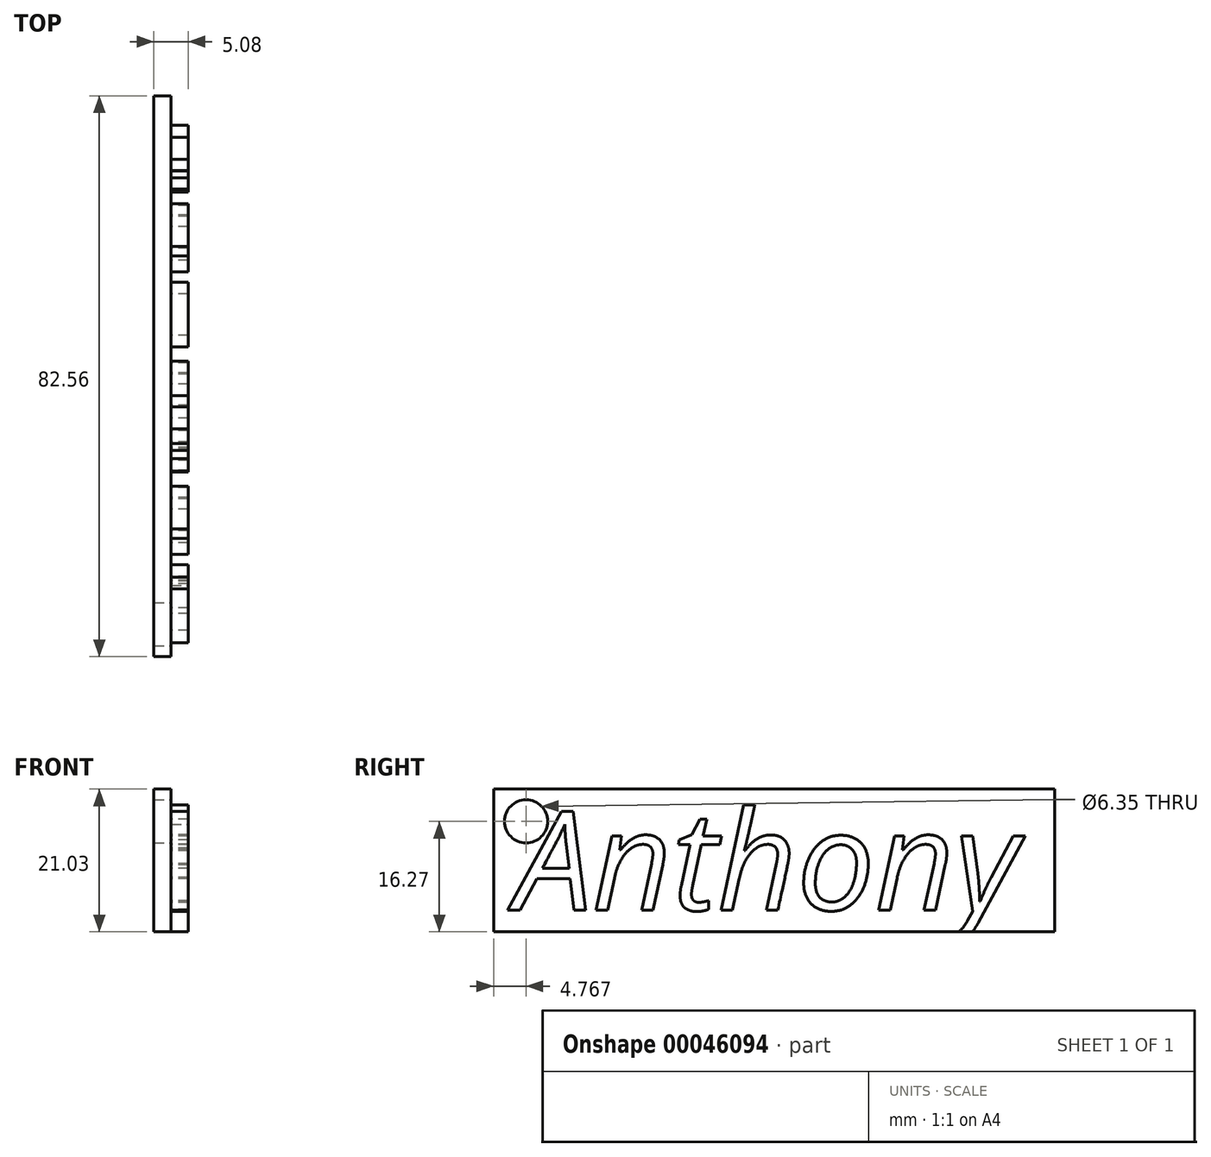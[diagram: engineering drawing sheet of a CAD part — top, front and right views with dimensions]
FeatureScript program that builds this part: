
annotation { "Feature Type Name" : "Feature", "Feature Type Description" : "" }
export const myFeature = defineFeature(function(context is Context, id is Id, definition is map)
    precondition{}
    {
        {
            var Q0;
            Q0=qCreatedBy(makeId("Right.planeOp"),FACE);
            var sketch = newSketch(context, id + "F0", { "sketchPlane" : qUnion([Q0])});
            skLineSegment(sketch, "E0", {"start": v(-41.27, 17.85) * mm, "end": v(-41.27, -3.18) * mm});
            skLineSegment(sketch, "E1", {"start": v(-41.27, -3.18) * mm, "end": v(41.27, -3.18) * mm});
            skLineSegment(sketch, "E2", {"start": v(41.27, -3.18) * mm, "end": v(41.27, 17.85) * mm});
            skLineSegment(sketch, "E3", {"start": v(41.27, 17.85) * mm, "end": v(-41.27, 17.85) * mm});
            skText(sketch, "E4", { "text": "Anthony ", "fontName": "OpenSans-Italic.ttf"});
            skPoint(sketch, "E5", {"position": v(0, -3.18) * mm});
            skPoint(sketch, "E6", {"position": v(41.27, 7.34) * mm});
            skPoint(sketch, "E7", {"position": v(38.1, 7.34) * mm});
            skCircle(sketch, "E8", {"center": v(-36.51, 13.09) * mm, "radius": 3.18 * mm});
            const initialGuessF0  = {"E4": [-0.0381, 0, 1, 0, 0.01468]};
            skSetInitialGuess(sketch, initialGuessF0);
            skSolve(sketch);
        }
        {
            var Q0;
            Q0=makeQuery(id+"F0.imprint","IMPRINT",FACE,{"disambiguationData":[TD([[makeQuery(id+"F0.imprint","IMPRINT",EDGE,{"derivedFrom":sQuery(id+"F0.wireOp",EDGE,"E4.sketch_text.stroke-33")}),-1.0]])]});
            var Q1;
            Q1=makeQuery(id+"F0.imprint","IMPRINT",FACE,{"disambiguationData":[TD([[makeQuery(id+"F0.imprint","IMPRINT",EDGE,{"derivedFrom":sQuery(id+"F0.wireOp",EDGE,"E0")}),1.0]])]});
            var Q2;
            Q2=makeQuery(id+"F0.imprint","IMPRINT",FACE,{"disambiguationData":[TD([[makeQuery(id+"F0.imprint","IMPRINT",EDGE,{"derivedFrom":sQuery(id+"F0.wireOp",EDGE,"E4.sketch_text.stroke-0")}),-1.0]])]});
            var Q3;
            Q3=makeQuery(id+"F0.imprint","IMPRINT",FACE,{"disambiguationData":[TD([[makeQuery(id+"F0.imprint","IMPRINT",EDGE,{"derivedFrom":sQuery(id+"F0.wireOp",EDGE,"E4.sketch_text.stroke-8")}),1.0]])]});
            var Q4;
            Q4=makeQuery(id+"F0.imprint","IMPRINT",FACE,{"disambiguationData":[TD([[makeQuery(id+"F0.imprint","IMPRINT",EDGE,{"derivedFrom":sQuery(id+"F0.wireOp",EDGE,"E4.sketch_text.stroke-13")}),-1.0]])]});
            var Q5;
            Q5=makeQuery(id+"F0.imprint","IMPRINT",FACE,{"disambiguationData":[TD([[makeQuery(id+"F0.imprint","IMPRINT",EDGE,{"derivedFrom":sQuery(id+"F0.wireOp",EDGE,"E4.sketch_text.stroke-54")}),-1.0]])]});
            var Q6;
            Q6=makeQuery(id+"F0.imprint","IMPRINT",FACE,{"disambiguationData":[TD([[makeQuery(id+"F0.imprint","IMPRINT",EDGE,{"derivedFrom":sQuery(id+"F0.wireOp",EDGE,"E4.sketch_text.stroke-76")}),-1.0]])]});
            var Q7;
            Q7=makeQuery(id+"F0.imprint","IMPRINT",FACE,{"disambiguationData":[TD([[makeQuery(id+"F0.imprint","IMPRINT",EDGE,{"derivedFrom":sQuery(id+"F0.wireOp",EDGE,"E4.sketch_text.stroke-86")}),1.0]])]});
            var Q8;
            Q8=makeQuery(id+"F0.imprint","IMPRINT",FACE,{"disambiguationData":[TD([[makeQuery(id+"F0.imprint","IMPRINT",EDGE,{"derivedFrom":sQuery(id+"F0.wireOp",EDGE,"E4.sketch_text.stroke-96")}),-1.0]])]});
            var Q9;
            Q9=makeQuery(id+"F0.imprint","IMPRINT",FACE,{"disambiguationData":[TD([[makeQuery(id+"F0.imprint","IMPRINT",EDGE,{"derivedFrom":sQuery(id+"F0.wireOp",EDGE,"E4.sketch_text.stroke-116")}),-1.0]])]});
            extrude(context, id + "F1", {"entities" : qUnion([Q0, Q1, Q2, Q3, Q4, Q5, Q6, Q7, Q8, Q9]), "oppositeDirection" : true, "depth" : 2.54 * mm});
        }
        {
            var Q0;
            Q0=makeQuery(id+"F0.imprint","IMPRINT",FACE,{"disambiguationData":[TD([[makeQuery(id+"F0.imprint","IMPRINT",EDGE,{"derivedFrom":sQuery(id+"F0.wireOp",EDGE,"E4.sketch_text.stroke-0")}),-1.0]])]});
            var Q1;
            Q1=makeQuery(id+"F0.imprint","IMPRINT",FACE,{"disambiguationData":[TD([[makeQuery(id+"F0.imprint","IMPRINT",EDGE,{"derivedFrom":sQuery(id+"F0.wireOp",EDGE,"E4.sketch_text.stroke-13")}),-1.0]])]});
            var Q2;
            Q2=makeQuery(id+"F0.imprint","IMPRINT",FACE,{"disambiguationData":[TD([[makeQuery(id+"F0.imprint","IMPRINT",EDGE,{"derivedFrom":sQuery(id+"F0.wireOp",EDGE,"E4.sketch_text.stroke-33")}),-1.0]])]});
            var Q3;
            Q3=makeQuery(id+"F0.imprint","IMPRINT",FACE,{"disambiguationData":[TD([[makeQuery(id+"F0.imprint","IMPRINT",EDGE,{"derivedFrom":sQuery(id+"F0.wireOp",EDGE,"E4.sketch_text.stroke-54")}),-1.0]])]});
            var Q4;
            Q4=makeQuery(id+"F0.imprint","IMPRINT",FACE,{"disambiguationData":[TD([[makeQuery(id+"F0.imprint","IMPRINT",EDGE,{"derivedFrom":sQuery(id+"F0.wireOp",EDGE,"E4.sketch_text.stroke-76")}),-1.0]])]});
            var Q5;
            Q5=makeQuery(id+"F0.imprint","IMPRINT",FACE,{"disambiguationData":[TD([[makeQuery(id+"F0.imprint","IMPRINT",EDGE,{"derivedFrom":sQuery(id+"F0.wireOp",EDGE,"E4.sketch_text.stroke-96")}),-1.0]])]});
            var Q6;
            Q6=makeQuery(id+"F0.imprint","IMPRINT",FACE,{"disambiguationData":[TD([[makeQuery(id+"F0.imprint","IMPRINT",EDGE,{"derivedFrom":sQuery(id+"F0.wireOp",EDGE,"E4.sketch_text.stroke-116")}),-1.0]])]});
            extrude(context, id + "F2", {"entities" : qUnion([Q0, Q1, Q2, Q3, Q4, Q5, Q6]), "operationType" : NewBodyOperationType.ADD, "depth" : 2.54 * mm});
        }
    });
